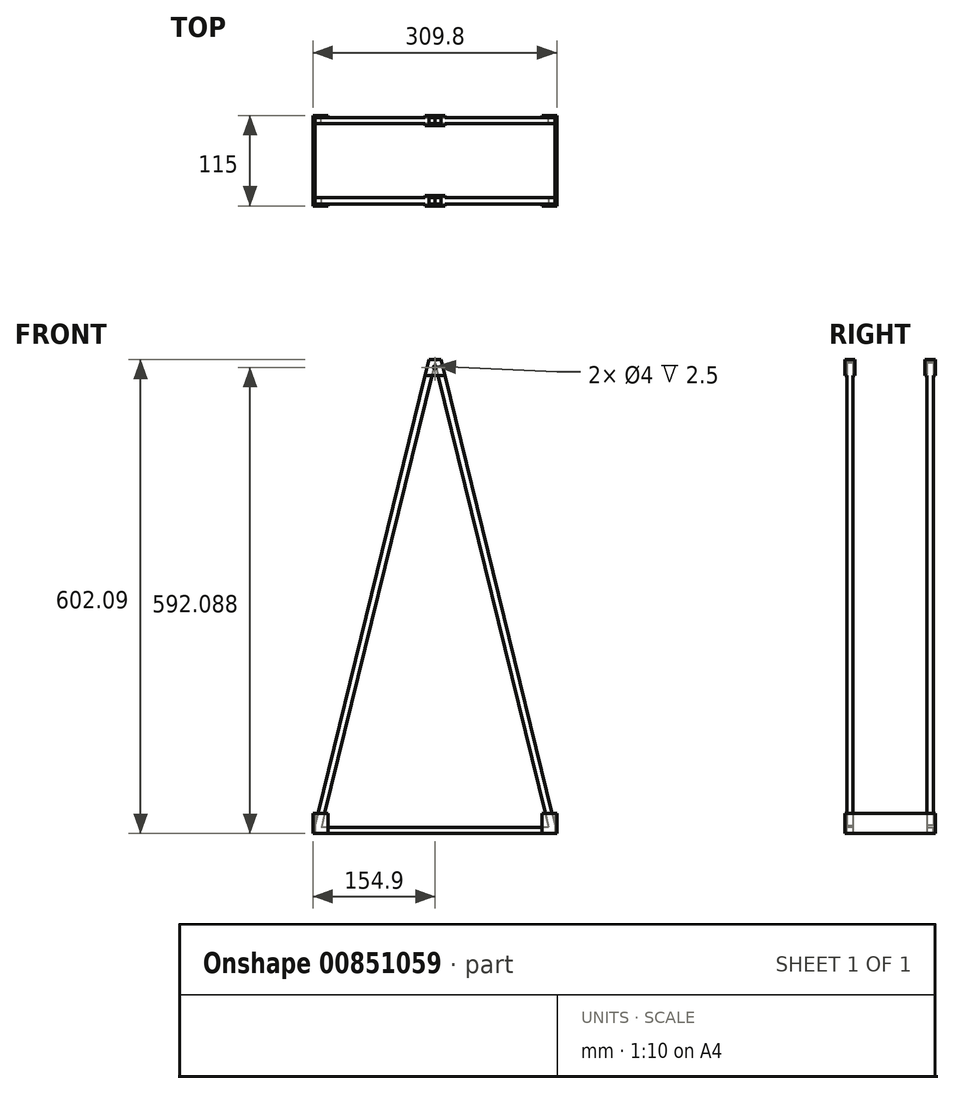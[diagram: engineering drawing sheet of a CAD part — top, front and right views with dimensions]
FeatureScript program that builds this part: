
annotation { "Feature Type Name" : "Feature", "Feature Type Description" : "" }
export const myFeature = defineFeature(function(context is Context, id is Id, definition is map)
    precondition{}
    {
        {
            var Q0;
            Q0=qCreatedBy(makeId("Top.planeOp"),FACE);
            var sketch = newSketch(context, id + "F0", { "sketchPlane" : qUnion([Q0])});
            skLineSegment(sketch, "E0.bottom", {"start": v(152.4, 55) * mm, "end": v(-152.4, 55) * mm});
            skLineSegment(sketch, "E0.top", {"start": v(152.4, -55) * mm, "end": v(-152.4, -55) * mm});
            skLineSegment(sketch, "E0.left", {"start": v(152.4, 55) * mm, "end": v(152.4, -55) * mm});
            skLineSegment(sketch, "E0.right", {"start": v(-152.4, 55) * mm, "end": v(-152.4, -55) * mm});
            skPoint(sketch, "E0.middle", {"position": v(0, 0) * mm});
            skLineSegment(sketch, "E1", {"start": v(152.4, 47) * mm, "end": v(-152.4, 47) * mm});
            skLineSegment(sketch, "E2", {"start": v(-152.4, -47) * mm, "end": v(152.4, -47) * mm});
            skLineSegment(sketch, "E3.bottom", {"start": v(-152.4, 55) * mm, "end": v(-154.9, 55) * mm});
            skLineSegment(sketch, "E3.top", {"start": v(-152.4, -55) * mm, "end": v(-154.9, -55) * mm});
            skLineSegment(sketch, "E3.right", {"start": v(-154.9, 55) * mm, "end": v(-154.9, -55) * mm});
            skLineSegment(sketch, "E4.bottom", {"start": v(152.4, 55) * mm, "end": v(154.9, 55) * mm});
            skLineSegment(sketch, "E4.top", {"start": v(152.4, -55) * mm, "end": v(154.9, -55) * mm});
            skLineSegment(sketch, "E4.right", {"start": v(154.9, 55) * mm, "end": v(154.9, -55) * mm});
            skSolve(sketch);
        }
        {
            var Q0;
            {var subQ0=sQuery(id+"F0.wireOp",EDGE,"E0.bottom");Q0=makeQuery(id+"F0.imprint","IMPRINT",FACE,{"disambiguationData":[TD([[makeQuery(id+"F0.imprint","IMPRINT",EDGE,{"derivedFrom":subQ0}),1.0]])]});}
            var Q1;
            {var subQ0=sQuery(id+"F0.wireOp",EDGE,"E0.top");Q1=makeQuery(id+"F0.imprint","IMPRINT",FACE,{"disambiguationData":[TD([[makeQuery(id+"F0.imprint","IMPRINT",EDGE,{"derivedFrom":subQ0}),-1.0]])]});}
            extrude(context, id + "F1", {"entities" : qUnion([Q0, Q1]), "depth" : 8 * mm, "offsetDistance" : 25 * mm});
        }
        {
            var Q0;
            {var subQ3=sQuery(id+"F0.wireOp",EDGE,"E3.bottom");Q0=makeQuery(id+"F0.imprint","IMPRINT",FACE,{"disambiguationData":[TD([[makeQuery(id+"F0.imprint","IMPRINT",EDGE,{"derivedFrom":subQ3}),1.0]])]});}
            var Q1;
            {var subQ3=sQuery(id+"F0.wireOp",EDGE,"E4.bottom");Q1=makeQuery(id+"F0.imprint","IMPRINT",FACE,{"disambiguationData":[TD([[makeQuery(id+"F0.imprint","IMPRINT",EDGE,{"derivedFrom":subQ3}),-1.0]])]});}
            extrude(context, id + "F2", {"entities" : qUnion([Q0, Q1]), "operationType" : NewBodyOperationType.ADD, "depth" : 25.4 * mm, "offsetDistance" : 25 * mm});
        }
        {
            var Q0;
            Q0=makeQuery(id+"F2.boolean.opBoolean","MERGE",FACE,{"derivedFrom":[makeQuery(id+"F1.opExtrude","SWEPT_FACE",FACE,{"disambiguationData":[OSD([sQuery(id+"F0.wireOp",EDGE,"E0.top")])]}),makeQuery(id+"F2.opExtrude","SWEPT_FACE",FACE,{"disambiguationData":[OSD([sQuery(id+"F0.wireOp",EDGE,"E3.top")])]}),makeQuery(id+"F2.opExtrude","SWEPT_FACE",FACE,{"disambiguationData":[OSD([sQuery(id+"F0.wireOp",EDGE,"E4.top")])]})]});
            var sketch = newSketch(context, id + "F3", { "sketchPlane" : qUnion([Q0])});
            skLineSegment(sketch, "E5.bottom", {"start": v(-154.9, 0) * mm, "end": v(-135.85, 0) * mm});
            skLineSegment(sketch, "E5.top", {"start": v(-154.9, 25.4) * mm, "end": v(-135.85, 25.4) * mm});
            skLineSegment(sketch, "E5.left", {"start": v(-154.9, 0) * mm, "end": v(-154.9, 25.4) * mm});
            skLineSegment(sketch, "E5.right", {"start": v(-135.85, 0) * mm, "end": v(-135.85, 25.4) * mm});
            skLineSegment(sketch, "E6", {"start": v(0, 0) * mm, "end": v(0, 8) * mm});
            skLineSegment(sketch, "E7.MirrorCS", {"start": v(154.9, 0) * mm, "end": v(154.9, 25.4) * mm});
            skLineSegment(sketch, "E8.MirrorCS", {"start": v(154.9, 25.4) * mm, "end": v(135.85, 25.4) * mm});
            skLineSegment(sketch, "E9.MirrorCS", {"start": v(135.85, 0) * mm, "end": v(135.85, 25.4) * mm});
            skLineSegment(sketch, "E10.MirrorCS", {"start": v(154.9, 0) * mm, "end": v(135.85, 0) * mm});
            skSolve(sketch);
        }
        {
            var Q0;
            Q0 = qSketchRegion(id + "F3", true);
            extrude(context, id + "F4", {"entities" : qUnion([Q0]), "operationType" : NewBodyOperationType.ADD, "depth" : 2.5 * mm, "offsetDistance" : 25 * mm});
        }
        {
            var Q0;
            Q0=makeQuery(id+"F1.opExtrude","SWEPT_BODY",BODY,{"disambiguationData":[OSD([sQuery(id+"F0.wireOp",EDGE,"E0.bottom"),sQuery(id+"F0.wireOp",EDGE,"E1"),sQuery(id+"F0.wireOp",EDGE,"E0.right"),sQuery(id+"F0.wireOp",EDGE,"E0.left")])]});
            var Q1;
            Q1=qCreatedBy(makeId("Front.planeOp"),FACE);
            mirror(context, id + "F5", {"operationType" : NewBodyOperationType.ADD, "entities" : qUnion([Q0]), "mirrorPlane" : qUnion([Q1])});
        }
        {
            var Q0;
            Q0=makeQuery(id+"F1.opExtrude","CAP_FACE",FACE,{"disambiguationData":[OSD([sQuery(id+"F0.wireOp",EDGE,"E0.top"),sQuery(id+"F0.wireOp",EDGE,"E2"),sQuery(id+"F0.wireOp",EDGE,"E0.right"),sQuery(id+"F0.wireOp",EDGE,"E0.left")])],"isStart":false});
            var sketch = newSketch(context, id + "F6", { "sketchPlane" : qUnion([Q0])});
            skLineSegment(sketch, "E11.bottom", {"start": v(-152.4, -47) * mm, "end": v(-144.4, -47) * mm});
            skLineSegment(sketch, "E11.top", {"start": v(-152.4, -55) * mm, "end": v(-144.4, -55) * mm});
            skLineSegment(sketch, "E11.left", {"start": v(-152.4, -47) * mm, "end": v(-152.4, -55) * mm});
            skLineSegment(sketch, "E11.right", {"start": v(-144.4, -47) * mm, "end": v(-144.4, -55) * mm});
            skLineSegment(sketch, "E12.bottom", {"start": v(152.4, -47) * mm, "end": v(144.4, -47) * mm});
            skLineSegment(sketch, "E12.top", {"start": v(152.4, -55) * mm, "end": v(144.4, -55) * mm});
            skLineSegment(sketch, "E12.left", {"start": v(152.4, -47) * mm, "end": v(152.4, -55) * mm});
            skLineSegment(sketch, "E12.right", {"start": v(144.4, -47) * mm, "end": v(144.4, -55) * mm});
            skSolve(sketch);
        }
        {
            var Q0;
            Q0=makeQuery(id+"F6.imprint","IMPRINT",FACE,{"disambiguationData":[TD([[makeQuery(id+"F6.imprint","IMPRINT",EDGE,{"derivedFrom":sQuery(id+"F6.wireOp",EDGE,"E12.bottom")}),-1.0]])]});
            extrude(context, id + "F7", {"entities" : qUnion([Q0]), "operationType" : NewBodyOperationType.ADD, "depth" : 25 * mm, "offsetDistance" : 25 * mm});
        }
        {
            var Q0;
            Q0=makeQuery(id+"F7.boolean.opBoolean","MERGE",FACE,{"derivedFrom":[makeQuery(id+"F1.opExtrude","SWEPT_FACE",FACE,{"disambiguationData":[OSD([sQuery(id+"F0.wireOp",EDGE,"E2")])]}),makeQuery(id+"F7.opExtrude","SWEPT_FACE",FACE,{"disambiguationData":[OSD([sQuery(id+"F6.wireOp",EDGE,"E12.bottom")])]})]});
            var sketch = newSketch(context, id + "F8", { "sketchPlane" : qUnion([Q0])});
            skLineSegment(sketch, "E13", {"start": v(-144.4, 8) * mm, "end": v(-152.4, 8) * mm});
            skLineSegment(sketch, "E14", {"start": v(-144.4, 8) * mm, "end": v(-152.4, 9.96) * mm});
            skLineSegment(sketch, "E15", {"start": v(-144.4, 8) * mm, "end": v(-140.63, 23.4) * mm});
            skLineSegment(sketch, "E16", {"start": v(-144.4, 8) * mm, "end": v(-139.04, 8) * mm});
            skSolve(sketch);
        }
        {
            var Q0;
            {var subQ4=sQuery(id+"F8.wireOp",EDGE,"E14");Q0=makeQuery(id+"F8.imprint","IMPRINT",FACE,{"disambiguationData":[TD([[makeQuery(id+"F8.imprint","IMPRINT",EDGE,{"derivedFrom":subQ4}),-1.0]])]});}
            extrude(context, id + "F9", {"entities" : qUnion([Q0]), "operationType" : NewBodyOperationType.REMOVE, "oppositeDirection" : true, "depth" : 8 * mm, "offsetDistance" : 25 * mm});
        }
        {
            var Q0;
            Q0=makeQuery(id+"F1.opExtrude","SWEPT_BODY",BODY,{"disambiguationData":[OSD([sQuery(id+"F0.wireOp",EDGE,"E0.bottom"),sQuery(id+"F0.wireOp",EDGE,"E1"),sQuery(id+"F0.wireOp",EDGE,"E0.right"),sQuery(id+"F0.wireOp",EDGE,"E0.left")])]});
            var Q1;
            Q1=qCreatedBy(makeId("Front.planeOp"),FACE);
            mirror(context, id + "F10", {"operationType" : NewBodyOperationType.ADD, "entities" : qUnion([Q0]), "mirrorPlane" : qUnion([Q1])});
        }
        {
            var Q0;
            Q0=makeQuery(id+"F1.opExtrude","SWEPT_BODY",BODY,{"disambiguationData":[OSD([sQuery(id+"F0.wireOp",EDGE,"E0.bottom"),sQuery(id+"F0.wireOp",EDGE,"E1"),sQuery(id+"F0.wireOp",EDGE,"E0.right"),sQuery(id+"F0.wireOp",EDGE,"E0.left")])]});
            var Q1;
            Q1=qCreatedBy(makeId("Right.planeOp"),FACE);
            mirror(context, id + "F11", {"operationType" : NewBodyOperationType.ADD, "entities" : qUnion([Q0]), "mirrorPlane" : qUnion([Q1])});
        }
        {
            var Q0;
            Q0=makeQuery(id+"F10.opPattern","COPY",FACE,{"derivedFrom":makeQuery(id+"F9.boolean.opBoolean","COPY",FACE,{"derivedFrom":makeQuery(id+"F9.opExtrude","SWEPT_FACE",FACE,{"disambiguationData":[OSD([sQuery(id+"F8.wireOp",EDGE,"E14")])]})}),"instanceName":"1"});
            var Q1;
            Q1=makeQuery(id+"F9.boolean.opBoolean","COPY",FACE,{"derivedFrom":makeQuery(id+"F9.opExtrude","SWEPT_FACE",FACE,{"disambiguationData":[OSD([sQuery(id+"F8.wireOp",EDGE,"E14")])]})});
            extrude(context, id + "F12", {"entities" : qUnion([Q0, Q1]), "operationType" : NewBodyOperationType.ADD, "depth" : 609.6 * mm, "offsetDistance" : 25 * mm});
        }
        {
            var Q0;
            Q0=makeQuery(id+"F11.opPattern","COPY",FACE,{"derivedFrom":makeQuery(id+"F10.opPattern","COPY",FACE,{"derivedFrom":makeQuery(id+"F9.boolean.opBoolean","COPY",FACE,{"derivedFrom":makeQuery(id+"F9.opExtrude","SWEPT_FACE",FACE,{"disambiguationData":[OSD([sQuery(id+"F8.wireOp",EDGE,"E14")])]})}),"instanceName":"1"}),"instanceName":"1"});
            var Q1;
            Q1=makeQuery(id+"F11.opPattern","COPY",FACE,{"derivedFrom":makeQuery(id+"F9.boolean.opBoolean","COPY",FACE,{"derivedFrom":makeQuery(id+"F9.opExtrude","SWEPT_FACE",FACE,{"disambiguationData":[OSD([sQuery(id+"F8.wireOp",EDGE,"E14")])]})}),"instanceName":"1"});
            extrude(context, id + "F13", {"entities" : qUnion([Q0, Q1]), "operationType" : NewBodyOperationType.ADD, "depth" : 609.6 * mm, "offsetDistance" : 25 * mm});
        }
        {
            var Q0;
            {var subQ0=sQuery(id+"F8.wireOp",EDGE,"E14");var subQ1=makeQuery(id+"F10.opPattern","COPY",EDGE,{"derivedFrom":makeQuery(id+"F9.boolean.opBoolean","COPY",EDGE,{"derivedFrom":makeQuery(id+"F9.opExtrude","CAP_EDGE",EDGE,{"disambiguationData":[OSD([subQ0])],"isStart":false})}),"instanceName":"1"});Q0=makeQuery(id+"F13.boolean.opBoolean","MERGE",FACE,{"derivedFrom":[makeQuery(id+"F12.opExtrude","SWEPT_FACE",FACE,{"disambiguationData":[OSD([subQ0]),TDD([subQ1])]}),makeQuery(id+"F13.opExtrude","SWEPT_FACE",FACE,{"disambiguationData":[OSD([subQ0]),TDD([makeQuery(id+"F11.opPattern","COPY",EDGE,{"derivedFrom":subQ1,"instanceName":"1"})])]})]});}
            var sketch = newSketch(context, id + "F14", { "sketchPlane" : qUnion([Q0])});
            skLineSegment(sketch, "E17", {"start": v(-7.5, 602.09) * mm, "end": v(7.5, 602.09) * mm});
            skLineSegment(sketch, "E18", {"start": v(7.5, 602.09) * mm, "end": v(12.5, 581.68) * mm});
            skLineSegment(sketch, "E19", {"start": v(-7.5, 602.09) * mm, "end": v(-12.5, 581.68) * mm});
            skLineSegment(sketch, "E20", {"start": v(-12.5, 581.68) * mm, "end": v(12.5, 581.68) * mm});
            skSolve(sketch);
        }
        {
            var Q0;
            Q0 = qSketchRegion(id + "F14", true);
            extrude(context, id + "F15", {"entities" : qUnion([Q0]), "operationType" : NewBodyOperationType.ADD, "depth" : 2.5 * mm, "offsetDistance" : 25 * mm});
        }
        {
            var Q0;
            {var subQ0=sQuery(id+"F8.wireOp",EDGE,"E14");var subQ1=makeQuery(id+"F10.opPattern","COPY",EDGE,{"derivedFrom":makeQuery(id+"F9.boolean.opBoolean","COPY",EDGE,{"derivedFrom":makeQuery(id+"F9.opExtrude","CAP_EDGE",EDGE,{"disambiguationData":[OSD([subQ0])],"isStart":true})}),"instanceName":"1"});var subQ2=makeQuery(id+"F10.boolean.opBoolean","MERGE",FACE,{"derivedFrom":[makeQuery(id+"F1.opExtrude","SWEPT_FACE",FACE,{"disambiguationData":[OSD([sQuery(id+"F0.wireOp",EDGE,"E1")])]}),makeQuery(id+"F10.opPattern","COPY",FACE,{"derivedFrom":makeQuery(id+"F7.boolean.opBoolean","MERGE",FACE,{"derivedFrom":[makeQuery(id+"F1.opExtrude","SWEPT_FACE",FACE,{"disambiguationData":[OSD([sQuery(id+"F0.wireOp",EDGE,"E2")])]}),makeQuery(id+"F7.opExtrude","SWEPT_FACE",FACE,{"disambiguationData":[OSD([sQuery(id+"F6.wireOp",EDGE,"E12.bottom")])]})]}),"instanceName":"1"})]});Q0=makeQuery(id+"F13.boolean.opBoolean","MERGE",FACE,{"derivedFrom":[makeQuery(id+"F12.boolean.opBoolean","MERGE",FACE,{"derivedFrom":[makeQuery(id+"F11.boolean.opBoolean","MERGE",FACE,{"derivedFrom":[subQ2,makeQuery(id+"F11.opPattern","COPY",FACE,{"derivedFrom":subQ2,"instanceName":"1"})]}),makeQuery(id+"F12.opExtrude","SWEPT_FACE",FACE,{"disambiguationData":[OSD([subQ0]),TDD([subQ1])]})]}),makeQuery(id+"F13.opExtrude","SWEPT_FACE",FACE,{"disambiguationData":[OSD([subQ0]),TDD([makeQuery(id+"F11.opPattern","COPY",EDGE,{"derivedFrom":subQ1,"instanceName":"1"})])]})]});}
            var sketch = newSketch(context, id + "F16", { "sketchPlane" : qUnion([Q0])});
            skLineSegment(sketch, "E21", {"start": v(-7.5, 602.09) * mm, "end": v(7.5, 602.09) * mm});
            skLineSegment(sketch, "E22", {"start": v(7.5, 602.09) * mm, "end": v(12.5, 581.68) * mm});
            skLineSegment(sketch, "E23", {"start": v(12.5, 581.68) * mm, "end": v(-12.5, 581.68) * mm});
            skLineSegment(sketch, "E24", {"start": v(-12.5, 581.68) * mm, "end": v(-7.5, 602.09) * mm});
            skSolve(sketch);
        }
        {
            var Q0;
            Q0 = qSketchRegion(id + "F16", true);
            extrude(context, id + "F17", {"entities" : qUnion([Q0]), "operationType" : NewBodyOperationType.ADD, "depth" : 2.5 * mm, "offsetDistance" : 25 * mm});
        }
        {
            var Q0;
            Q0=makeQuery(id+"F15.opExtrude","CAP_FACE",FACE,{"disambiguationData":[OSD([sQuery(id+"F14.wireOp",EDGE,"E17"),sQuery(id+"F14.wireOp",EDGE,"E18"),sQuery(id+"F14.wireOp",EDGE,"E19"),sQuery(id+"F14.wireOp",EDGE,"E20")])],"isStart":false});
            var sketch = newSketch(context, id + "F18", { "sketchPlane" : qUnion([Q0])});
            skCircle(sketch, "E25", {"center": v(0, 592.09) * mm, "radius": 2 * mm});
            skPoint(sketch, "E25.centerSnap0", {"position": v(0, 602.09) * mm});
            skSolve(sketch);
        }
        {
            var Q0;
            Q0 = qSketchRegion(id + "F18", true);
            var Q1;
            Q1=makeQuery(id+"F17.opExtrude","CAP_FACE",FACE,{"disambiguationData":[OSD([sQuery(id+"F16.wireOp",EDGE,"E21"),sQuery(id+"F16.wireOp",EDGE,"E22"),sQuery(id+"F16.wireOp",EDGE,"E23"),sQuery(id+"F16.wireOp",EDGE,"E24")])],"isStart":false});
            extrude(context, id + "F19", {"entities" : qUnion([Q0]), "operationType" : NewBodyOperationType.REMOVE, "endBound" : BoundingType.UP_TO_SURFACE, "oppositeDirection" : true, "depth" : 25 * mm, "endBoundEntityFace" : qUnion([Q1]), "offsetDistance" : 25 * mm});
        }
        {
            var Q0;
            Q0=makeQuery(id+"F1.opExtrude","SWEPT_BODY",BODY,{"disambiguationData":[OSD([sQuery(id+"F0.wireOp",EDGE,"E0.bottom"),sQuery(id+"F0.wireOp",EDGE,"E1"),sQuery(id+"F0.wireOp",EDGE,"E0.right"),sQuery(id+"F0.wireOp",EDGE,"E0.left")])]});
            var Q1;
            Q1=qCreatedBy(makeId("Front.planeOp"),FACE);
            mirror(context, id + "F20", {"operationType" : NewBodyOperationType.ADD, "entities" : qUnion([Q0]), "mirrorPlane" : qUnion([Q1])});
        }
    });
